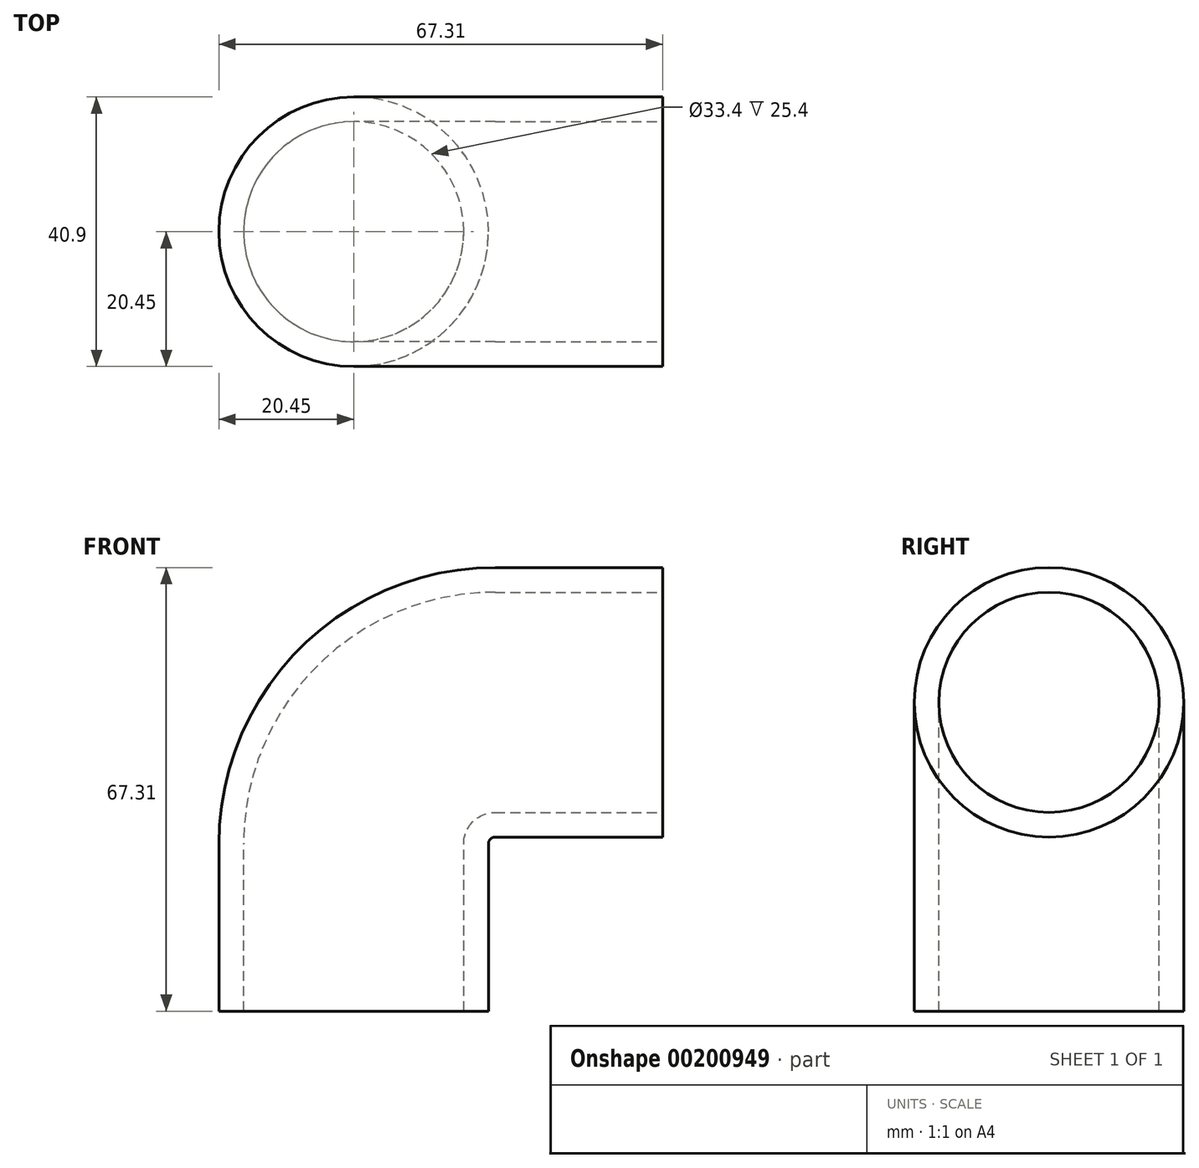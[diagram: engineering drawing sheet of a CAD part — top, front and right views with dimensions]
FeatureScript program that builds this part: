
annotation { "Feature Type Name" : "Feature", "Feature Type Description" : "" }
export const myFeature = defineFeature(function(context is Context, id is Id, definition is map)
    precondition{}
    {
        {
            var Q0;
            Q0=qCreatedBy(makeId("Top.planeOp"),FACE);
            var sketch = newSketch(context, id + "F0", { "sketchPlane" : qUnion([Q0])});
            skCircle(sketch, "E0", {"center": v(0, 0) * mm, "radius": 20.45 * mm});
            skCircle(sketch, "E1", {"center": v(0, 0) * mm, "radius": 16.7 * mm});
            skSolve(sketch);
        }
        {
            var Q0;
            Q0=qCreatedBy(makeId("Front.planeOp"),FACE);
            var sketch = newSketch(context, id + "F1", { "sketchPlane" : qUnion([Q0])});
            skLineSegment(sketch, "E2", {"start": v(20.45, 25.4) * mm, "end": v(20.45, 0) * mm});
            skLineSegment(sketch, "E3", {"start": v(46.86, 26.42) * mm, "end": v(21.46, 26.42) * mm});
            skArc(sketch, "E4", {"start": v(21.46, 26.42) * mm, "mid": v(20.74, 26.12) * mm, "end": v(20.45, 25.4) * mm});
            skSolve(sketch);
        }
        {
            var Q0;
            Q0=makeQuery(id+"F0.imprint","IMPRINT",FACE,{"disambiguationData":[TD([[makeQuery(id+"F0.imprint","IMPRINT",EDGE,{"derivedFrom":sQuery(id+"F0.wireOp",EDGE,"E0")}),1.0]])]});
            var Q1;
            Q1=sQuery(id+"F1.wireOp",EDGE,"E2");
            var Q2;
            Q2=sQuery(id+"F1.wireOp",EDGE,"E4");
            var Q3;
            Q3=sQuery(id+"F1.wireOp",EDGE,"E3");
            sweep(context, id + "F2", {"profiles" : qUnion([Q0]), "path" : qUnion([Q1, Q2, Q3])});
        }
    });
